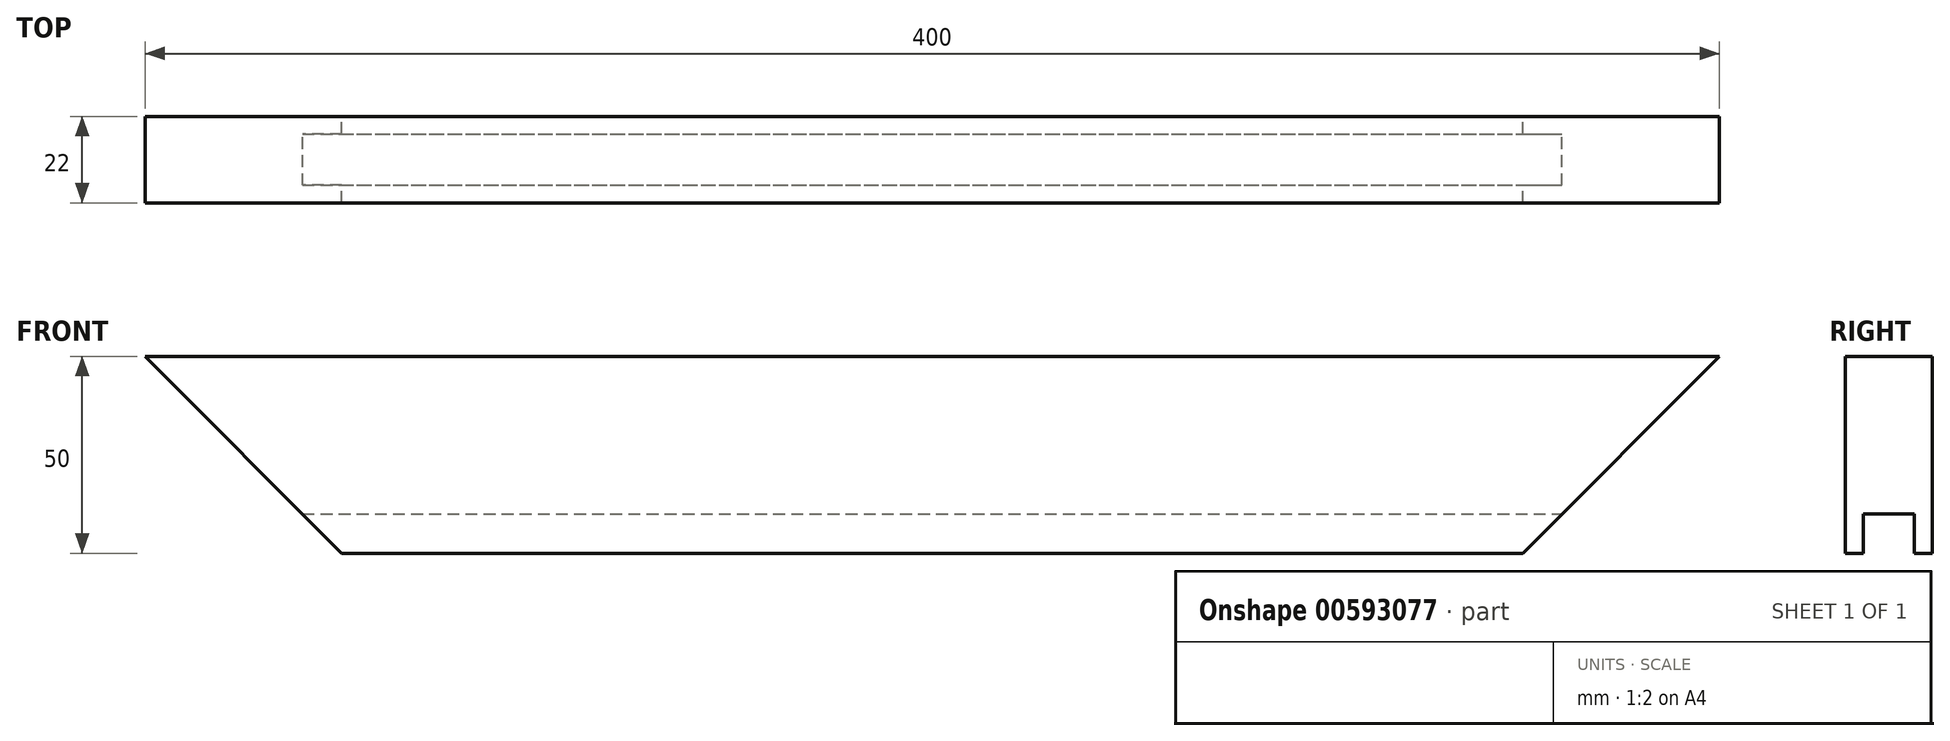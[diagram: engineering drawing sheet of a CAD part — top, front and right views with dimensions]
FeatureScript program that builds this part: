
annotation { "Feature Type Name" : "Feature", "Feature Type Description" : "" }
export const myFeature = defineFeature(function(context is Context, id is Id, definition is map)
    precondition{}
    {
        {
            var Q0;
            Q0=qCreatedBy(makeId("Front.planeOp"),FACE);
            var sketch = newSketch(context, id + "F0", { "sketchPlane" : qUnion([Q0])});
            skLineSegment(sketch, "E0.bottom", {"start": v(-200, 0) * mm, "end": v(200, 0) * mm});
            skLineSegment(sketch, "E0.top", {"start": v(-150, -50) * mm, "end": v(150, -50) * mm});
            skLineSegment(sketch, "E1", {"start": v(-200, 0) * mm, "end": v(-150, -50) * mm});
            skLineSegment(sketch, "E2", {"start": v(200, 0) * mm, "end": v(150, -50) * mm});
            skSolve(sketch);
        }
        {
            var Q0;
            Q0=qSketchRegion(id+"F0",true);
            extrude(context, id + "F1", {"entities" : qUnion([Q0]), "depth" : 22 * mm, "offsetDistance" : 25 * mm});
        }
        {
            var Q0;
            Q0=makeQuery(id+"F1.opExtrude","SWEPT_FACE",FACE,{"disambiguationData":[OSD([sQuery(id+"F0.wireOp",EDGE,"E0.top")])]});
            var sketch = newSketch(context, id + "F2", { "sketchPlane" : qUnion([Q0])});
            skLineSegment(sketch, "E3.bottom", {"start": v(-177.2, 17.5) * mm, "end": v(230.58, 17.5) * mm});
            skLineSegment(sketch, "E3.top", {"start": v(-177.2, 4.5) * mm, "end": v(230.58, 4.5) * mm});
            skLineSegment(sketch, "E3.left", {"start": v(-177.2, 17.5) * mm, "end": v(-177.2, 4.5) * mm});
            skLineSegment(sketch, "E3.right", {"start": v(230.58, 17.5) * mm, "end": v(230.58, 4.5) * mm});
            skSolve(sketch);
        }
        {
            var Q0;
            Q0 = qSketchRegion(id + "F2", true);
            extrude(context, id + "F3", {"entities" : qUnion([Q0]), "operationType" : NewBodyOperationType.REMOVE, "oppositeDirection" : true, "depth" : 10 * mm, "offsetDistance" : 25 * mm});
        }
    });
